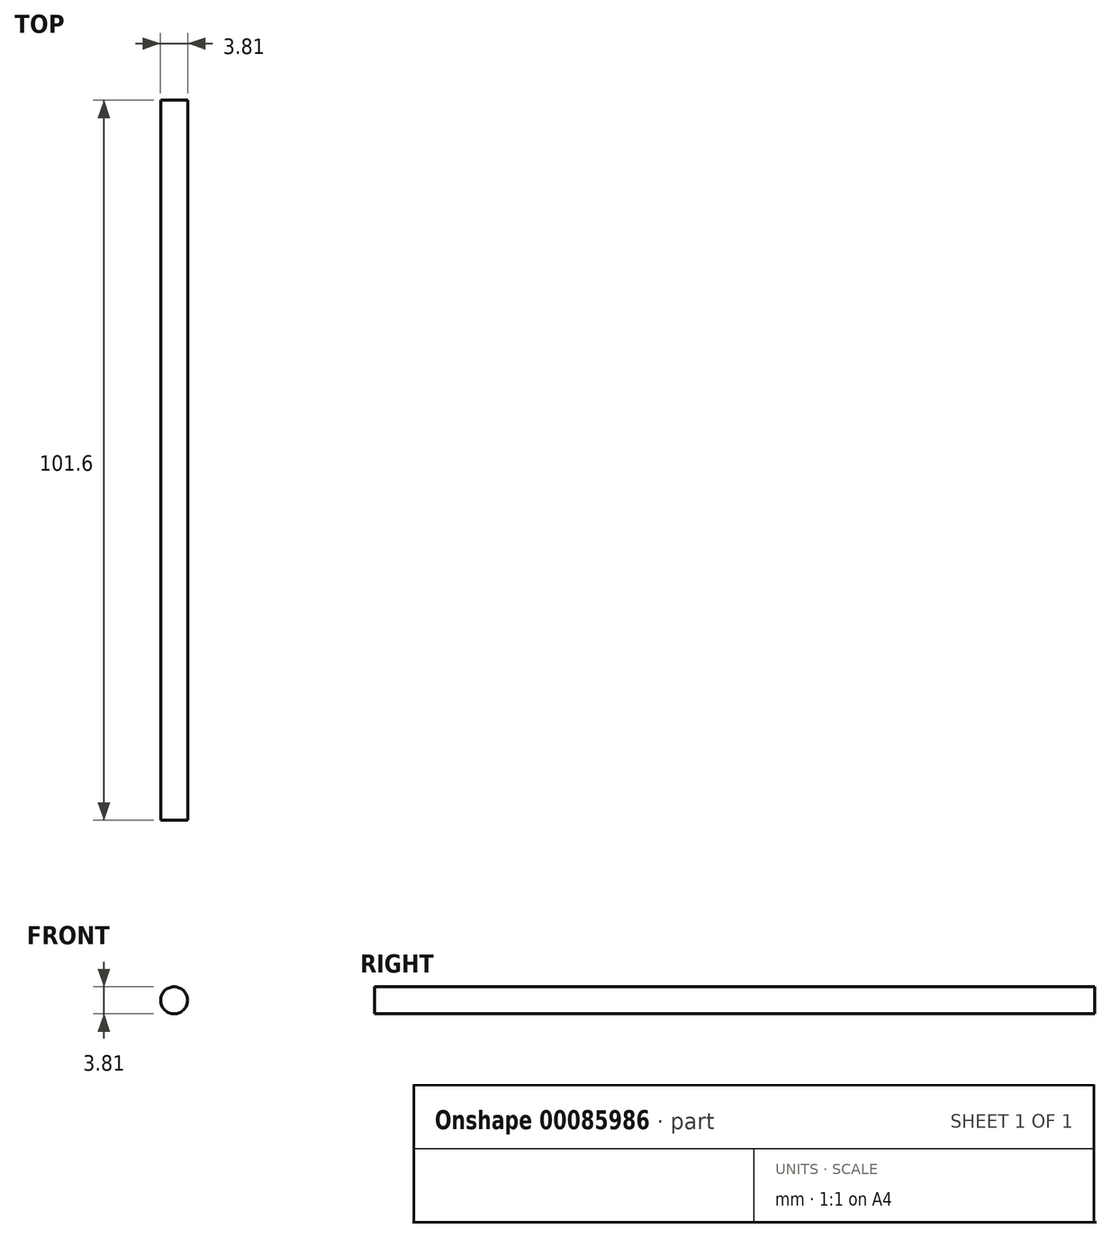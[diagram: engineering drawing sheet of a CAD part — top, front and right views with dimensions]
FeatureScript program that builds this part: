
annotation { "Feature Type Name" : "Feature", "Feature Type Description" : "" }
export const myFeature = defineFeature(function(context is Context, id is Id, definition is map)
    precondition{}
    {
        {
            var Q0;
            Q0=qCreatedBy(makeId("Front.planeOp"),FACE);
            var sketch = newSketch(context, id + "F0", { "sketchPlane" : qUnion([Q0])});
            skCircle(sketch, "E0", {"center": v(16.47, 14.96) * mm, "radius": 1.9 * mm});
            skSolve(sketch);
        }
        {
            var Q0;
            Q0 = qSketchRegion(id + "F0", true);
            extrude(context, id + "F1", {"entities" : qUnion([Q0]), "depth" : 101.6 * mm});
        }
    });
